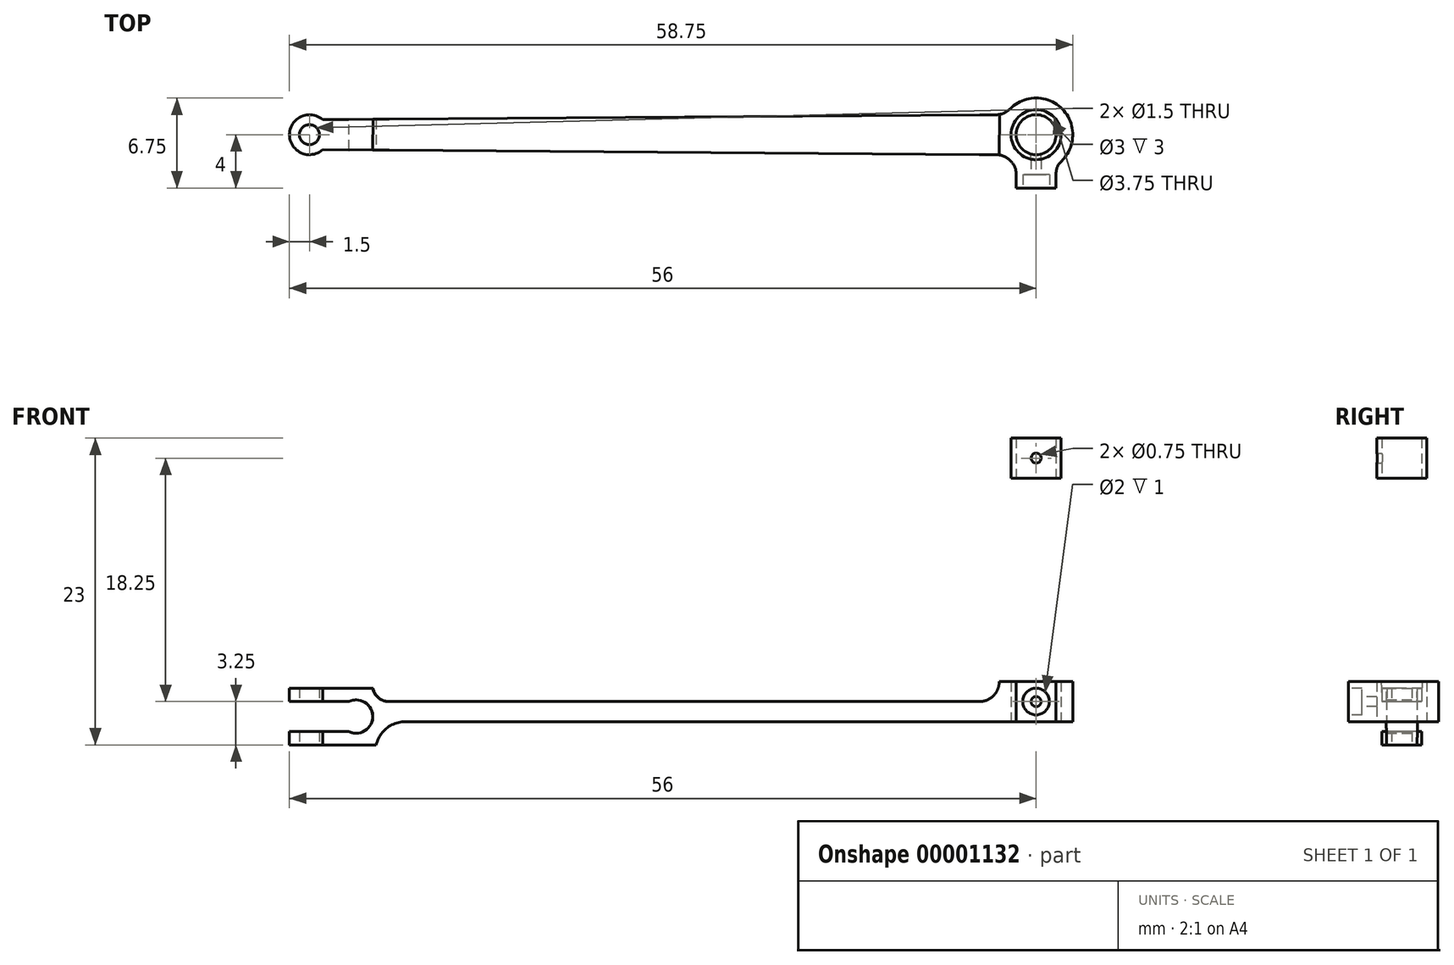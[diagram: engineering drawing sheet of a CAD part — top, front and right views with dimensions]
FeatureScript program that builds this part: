
annotation { "Feature Type Name" : "Feature", "Feature Type Description" : "" }
export const myFeature = defineFeature(function(context is Context, id is Id, definition is map)
    precondition{}
    {
        {
            var Q0;
            Q0=qCreatedBy(makeId("Top.planeOp"),FACE);
            var sketch = newSketch(context, id + "F0", { "sketchPlane" : qUnion([Q0])});
            skCircle(sketch, "E0", {"center": v(0, 0) * mm, "radius": 0.75 * mm});
            skCircle(sketch, "E1", {"center": v(54.5, 0) * mm, "radius": 1.88 * mm});
            skArc(sketch, "E2", {"start": v(1, 1.13) * mm, "mid": v(-1.5, 0) * mm, "end": v(1, -1.13) * mm});
            skArc(sketch, "E3", {"start": v(52.2, -1.5) * mm, "mid": v(52.56, -1.94) * mm, "end": v(53, -2.3) * mm});
            skLineSegment(sketch, "E4", {"start": v(1, 1.13) * mm, "end": v(52.2, 1.5) * mm});
            skLineSegment(sketch, "E5", {"start": v(1, -1.13) * mm, "end": v(52.2, -1.5) * mm});
            skLineSegment(sketch, "E6", {"start": v(53, -2.3) * mm, "end": v(53, -4) * mm});
            skLineSegment(sketch, "E7", {"start": v(53, -4) * mm, "end": v(56, -4) * mm});
            skLineSegment(sketch, "E8", {"start": v(56, -4) * mm, "end": v(56, -2.3) * mm});
            skPoint(sketch, "E9", {"position": v(54.5, -4) * mm});
            skArc(sketch, "E10.trimOffspring", {"start": v(56, -2.3) * mm, "mid": v(56.44, 1.94) * mm, "end": v(52.2, 1.5) * mm});
            skSolve(sketch);
        }
        {
            var Q0;
            Q0=makeQuery(id+"F0.imprint","IMPRINT",FACE,{"disambiguationData":[TD([[makeQuery(id+"F0.imprint","IMPRINT",EDGE,{"derivedFrom":sQuery(id+"F0.wireOp",EDGE,"E0")}),-1.0]])]});
            extrude(context, id + "F1", {"entities" : qUnion([Q0]), "depth" : 4.75 * mm});
        }
        {
            var Q0;
            Q0=makeQuery(id+"F1.opExtrude","CAP_FACE",FACE,{"disambiguationData":[OSD([sQuery(id+"F0.wireOp",EDGE,"E0"),sQuery(id+"F0.wireOp",EDGE,"E1"),sQuery(id+"F0.wireOp",EDGE,"E2"),sQuery(id+"F0.wireOp",EDGE,"E3"),sQuery(id+"F0.wireOp",EDGE,"E4"),sQuery(id+"F0.wireOp",EDGE,"E5"),sQuery(id+"F0.wireOp",EDGE,"E6"),sQuery(id+"F0.wireOp",EDGE,"E7"),sQuery(id+"F0.wireOp",EDGE,"E8"),sQuery(id+"F0.wireOp",EDGE,"E10.trimOffspring")])],"isStart":false});
            var sketch = newSketch(context, id + "F2", { "sketchPlane" : qUnion([Q0])});
            skLineSegment(sketch, "E11", {"start": v(51.74, -1.5) * mm, "end": v(51.76, 1.5) * mm});
            skLineSegment(sketch, "E12", {"start": v(4.74, -1.15) * mm, "end": v(4.76, 1.15) * mm});
            skSolve(sketch);
        }
        {
            var Q0;
            {var subQ2=sQuery(id+"F2.wireOp",EDGE,"E11");Q0=makeQuery(id+"F2.imprint","IMPRINT",FACE,{"disambiguationData":[TD([[makeQuery(id+"F2.imprint","IMPRINT",EDGE,{"derivedFrom":subQ2}),1.0]])]});}
            extrude(context, id + "F3", {"entities" : qUnion([Q0]), "operationType" : NewBodyOperationType.REMOVE, "oppositeDirection" : true, "depth" : 1.5 * mm});
        }
        {
            var Q0;
            {var subQ0=sQuery(id+"F0.wireOp",EDGE,"E0");var subQ1=sQuery(id+"F0.wireOp",EDGE,"E2");var subQ2=sQuery(id+"F0.wireOp",EDGE,"E4");var subQ3=sQuery(id+"F0.wireOp",EDGE,"E5");Q0=makeQuery(id+"F3.boolean.opBoolean","SPLIT",FACE,{"disambiguationData":[TD([makeQuery(id+"F1.opExtrude","SWEPT_FACE",FACE,{"disambiguationData":[OSD([subQ0])]})])],"derivedFrom":makeQuery(id+"F1.opExtrude","CAP_FACE",FACE,{"disambiguationData":[OSD([subQ0,sQuery(id+"F0.wireOp",EDGE,"E1"),subQ1,sQuery(id+"F0.wireOp",EDGE,"E3"),subQ2,subQ3,sQuery(id+"F0.wireOp",EDGE,"E6"),sQuery(id+"F0.wireOp",EDGE,"E7"),sQuery(id+"F0.wireOp",EDGE,"E8"),sQuery(id+"F0.wireOp",EDGE,"E10.trimOffspring")])],"isStart":false})});}
            extrude(context, id + "F4", {"entities" : qUnion([Q0]), "operationType" : NewBodyOperationType.REMOVE, "oppositeDirection" : true, "depth" : 0.5 * mm});
        }
        {
            var Q0;
            Q0=makeQuery(id+"F1.opExtrude","CAP_FACE",FACE,{"disambiguationData":[OSD([sQuery(id+"F0.wireOp",EDGE,"E0"),sQuery(id+"F0.wireOp",EDGE,"E1"),sQuery(id+"F0.wireOp",EDGE,"E2"),sQuery(id+"F0.wireOp",EDGE,"E3"),sQuery(id+"F0.wireOp",EDGE,"E4"),sQuery(id+"F0.wireOp",EDGE,"E5"),sQuery(id+"F0.wireOp",EDGE,"E6"),sQuery(id+"F0.wireOp",EDGE,"E7"),sQuery(id+"F0.wireOp",EDGE,"E8"),sQuery(id+"F0.wireOp",EDGE,"E10.trimOffspring")])],"isStart":true});
            var sketch = newSketch(context, id + "F5", { "sketchPlane" : qUnion([Q0])});
            skLineSegment(sketch, "E13", {"start": v(5, -1.15) * mm, "end": v(5, 1.15) * mm});
            skSolve(sketch);
        }
        {
            var Q0;
            {var subQ1=sQuery(id+"F5.wireOp",EDGE,"E13");Q0=makeQuery(id+"F5.imprint","IMPRINT",FACE,{"disambiguationData":[TD([[makeQuery(id+"F5.imprint","IMPRINT",EDGE,{"derivedFrom":subQ1}),-1.0]])]});}
            extrude(context, id + "F6", {"entities" : qUnion([Q0]), "operationType" : NewBodyOperationType.REMOVE, "oppositeDirection" : true, "depth" : 1.75 * mm});
        }
        {
            var Q0;
            Q0=makeQuery(id+"F3.boolean.opBoolean","COPY",EDGE,{"derivedFrom":makeQuery(id+"F3.opExtrude","CAP_EDGE",EDGE,{"disambiguationData":[OSD([sQuery(id+"F2.wireOp",EDGE,"E12")])],"isStart":false})});
            fillet(context, id + "F7", {"entities" : qUnion([Q0]), "radius" : 1.25 * mm, "tangentPropagation" : true, "allowEdgeOverflow" : false});
        }
        {
            var Q0;
            Q0=makeQuery(id+"F3.boolean.opBoolean","COPY",EDGE,{"derivedFrom":makeQuery(id+"F3.opExtrude","CAP_EDGE",EDGE,{"disambiguationData":[OSD([sQuery(id+"F2.wireOp",EDGE,"E11")])],"isStart":false})});
            fillet(context, id + "F8", {"entities" : qUnion([Q0]), "radius" : 1.5 * mm, "tangentPropagation" : true, "allowEdgeOverflow" : false});
        }
        {
            var Q0;
            Q0=makeQuery(id+"F6.boolean.opBoolean","COPY",EDGE,{"derivedFrom":makeQuery(id+"F6.opExtrude","CAP_EDGE",EDGE,{"disambiguationData":[OSD([sQuery(id+"F5.wireOp",EDGE,"E13")])],"isStart":false})});
            fillet(context, id + "F9", {"entities" : qUnion([Q0]), "radius" : 2.25 * mm, "tangentPropagation" : true, "allowEdgeOverflow" : false});
        }
        {
            var Q0;
            Q0=makeQuery(id+"F1.opExtrude","SWEPT_FACE",FACE,{"disambiguationData":[OSD([sQuery(id+"F0.wireOp",EDGE,"E4")])]});
            var sketch = newSketch(context, id + "F10", { "sketchPlane" : qUnion([Q0])});
            skLineSegment(sketch, "E14", {"start": v(-3.5, 4.25) * mm, "end": v(-3.5, 0) * mm, "construction": true});
            skPoint(sketch, "E15", {"position": v(-3.5, 2.12) * mm});
            skArc(sketch, "E16", {"start": v(-2.96, 3.25) * mm, "mid": v(-4.75, 2.12) * mm, "end": v(-2.96, 1) * mm});
            skLineSegment(sketch, "E17", {"start": v(-2.96, 3.25) * mm, "end": v(1.72, 3.25) * mm});
            skLineSegment(sketch, "E18", {"start": v(1.72, 3.25) * mm, "end": v(1.72, 1) * mm});
            skLineSegment(sketch, "E19", {"start": v(1.72, 1) * mm, "end": v(-2.96, 1) * mm});
            skPoint(sketch, "E20", {"position": v(1.72, 2.13) * mm});
            skSolve(sketch);
        }
        {
            var Q0;
            {var subQ5=sQuery(id+"F10.wireOp",EDGE,"E18");Q0=makeQuery(id+"F10.imprint","IMPRINT",FACE,{"disambiguationData":[TD([[makeQuery(id+"F10.imprint","IMPRINT",EDGE,{"derivedFrom":subQ5}),-1.0]])]});}
            var Q1;
            {var subQ5=sQuery(id+"F10.wireOp",EDGE,"E16");Q1=makeQuery(id+"F10.imprint","IMPRINT",FACE,{"disambiguationData":[TD([[makeQuery(id+"F10.imprint","IMPRINT",EDGE,{"derivedFrom":subQ5}),1.0]])]});}
            extrude(context, id + "F11", {"entities" : qUnion([Q0, Q1]), "operationType" : NewBodyOperationType.REMOVE, "endBound" : BoundingType.SYMMETRIC, "oppositeDirection" : true, "depth" : 25 * mm});
        }
        {
            var Q0;
            Q0=makeQuery(id+"F1.opExtrude","SWEPT_FACE",FACE,{"disambiguationData":[OSD([sQuery(id+"F0.wireOp",EDGE,"E7")])]});
            var sketch = newSketch(context, id + "F12", { "sketchPlane" : qUnion([Q0])});
            skPoint(sketch, "E21", {"position": v(53, 3.25) * mm});
            skPoint(sketch, "E22", {"position": v(54.5, 4.75) * mm});
            skCircle(sketch, "E23", {"center": v(54.5, 3.25) * mm, "radius": 1 * mm});
            skCircle(sketch, "E24", {"center": v(54.5, 3.25) * mm, "radius": 0.38 * mm});
            skSolve(sketch);
        }
        {
            var Q0;
            Q0=makeQuery(id+"F12.imprint","IMPRINT",FACE,{"disambiguationData":[TD([[makeQuery(id+"F12.imprint","IMPRINT",EDGE,{"derivedFrom":sQuery(id+"F12.wireOp",EDGE,"E23")}),1.0]])]});
            extrude(context, id + "F13", {"entities" : qUnion([Q0]), "operationType" : NewBodyOperationType.REMOVE, "oppositeDirection" : true, "depth" : 1 * mm});
        }
        {
            var Q0;
            Q0=makeQuery(id+"F13.boolean.opBoolean","SPLIT",FACE,{"disambiguationData":[TD([makeQuery(id+"F13.opExtrude","SWEPT_FACE",FACE,{"disambiguationData":[OSD([sQuery(id+"F12.wireOp",EDGE,"E24")])]})])],"derivedFrom":makeQuery(id+"F1.opExtrude","SWEPT_FACE",FACE,{"disambiguationData":[OSD([sQuery(id+"F0.wireOp",EDGE,"E7")])]})});
            var Q1;
            Q1=makeQuery(id+"F1.opExtrude","SWEPT_BODY",BODY,{"disambiguationData":[OSD([sQuery(id+"F0.wireOp",EDGE,"E0"),sQuery(id+"F0.wireOp",EDGE,"E1"),sQuery(id+"F0.wireOp",EDGE,"E2"),sQuery(id+"F0.wireOp",EDGE,"E3"),sQuery(id+"F0.wireOp",EDGE,"E4"),sQuery(id+"F0.wireOp",EDGE,"E5"),sQuery(id+"F0.wireOp",EDGE,"E6"),sQuery(id+"F0.wireOp",EDGE,"E7"),sQuery(id+"F0.wireOp",EDGE,"E8"),sQuery(id+"F0.wireOp",EDGE,"E10.trimOffspring")])]});
            extrude(context, id + "F14", {"entities" : qUnion([Q0]), "operationType" : NewBodyOperationType.REMOVE, "endBound" : BoundingType.UP_TO_BODY, "oppositeDirection" : true, "endBoundEntityBody" : qUnion([Q1]), "depth" : 25 * mm});
        }
        {
            var Q0;
            Q0=makeQuery(id+"F1.opExtrude","SWEPT_EDGE",EDGE,{"disambiguationData":[OSD([sQuery(id+"F0.wireOp",EDGE,"E3"),sQuery(id+"F0.wireOp",EDGE,"E6")])]});
            var Q1;
            Q1=makeQuery(id+"F1.opExtrude","SWEPT_EDGE",EDGE,{"disambiguationData":[OSD([sQuery(id+"F0.wireOp",EDGE,"E8"),sQuery(id+"F0.wireOp",EDGE,"E10.trimOffspring")])]});
            fillet(context, id + "F15", {"entities" : qUnion([Q0, Q1]), "radius" : 1.25 * mm, "tangentPropagation" : true, "allowEdgeOverflow" : false});
        }
        {
            var Q0;
            Q0=makeQuery(id+"F1.opExtrude","SWEPT_EDGE",EDGE,{"disambiguationData":[OSD([sQuery(id+"F0.wireOp",EDGE,"E4"),sQuery(id+"F0.wireOp",EDGE,"E10.trimOffspring")])]});
            var Q1;
            Q1=makeQuery(id+"F1.opExtrude","SWEPT_EDGE",EDGE,{"disambiguationData":[OSD([sQuery(id+"F0.wireOp",EDGE,"E3"),sQuery(id+"F0.wireOp",EDGE,"E5")])]});
            fillet(context, id + "F16", {"entities" : qUnion([Q0, Q1]), "radius" : 1.5 * mm, "tangentPropagation" : true, "allowEdgeOverflow" : false});
        }
        {
            var Q0;
            Q0=qCreatedBy(makeId("Top.planeOp"),FACE);
            cPlane(context, id + "F17", {"entities" : qUnion([Q0]), "cplaneType" : CPlaneType.OFFSET, "offset" : 20 * mm, "width" : 150 * mm, "height" : 150 * mm});
        }
        {
            var Q0;
            Q0=qCreatedBy(id+"F17.planeOp",FACE);
            var sketch = newSketch(context, id + "F18", { "sketchPlane" : qUnion([Q0])});
            skLineSegment(sketch, "E25", {"start": v(0, 0) * mm, "end": v(54.5, 0) * mm, "construction": true});
            skCircle(sketch, "E26", {"center": v(54.5, 0) * mm, "radius": 1.88 * mm});
            skCircle(sketch, "E27", {"center": v(54.5, 0) * mm, "radius": 1.5 * mm});
            skSolve(sketch);
        }
        {
            var Q0;
            Q0=makeQuery(id+"F18.imprint","IMPRINT",FACE,{"disambiguationData":[TD([[makeQuery(id+"F18.imprint","IMPRINT",EDGE,{"derivedFrom":sQuery(id+"F18.wireOp",EDGE,"E26")}),1.0]])]});
            extrude(context, id + "F19", {"entities" : qUnion([Q0]), "depth" : 3 * mm});
        }
        {
            var Q0;
            Q0=qCreatedBy(makeId("Front.planeOp"),FACE);
            var sketch = newSketch(context, id + "F20", { "sketchPlane" : qUnion([Q0])});
            skLineSegment(sketch, "E28", {"start": v(0, 0) * mm, "end": v(0, 21.5) * mm, "construction": true});
            skLineSegment(sketch, "E29", {"start": v(0, 21.5) * mm, "end": v(54.5, 21.5) * mm, "construction": true});
            skCircle(sketch, "E30", {"center": v(54.5, 21.5) * mm, "radius": 0.38 * mm});
            skSolve(sketch);
        }
        {
            var Q0;
            Q0=makeQuery(id+"F20.imprint","IMPRINT",FACE,{"disambiguationData":[TD([[makeQuery(id+"F20.imprint","IMPRINT",EDGE,{"derivedFrom":sQuery(id+"F20.wireOp",EDGE,"E30")}),1.0]])]});
            extrude(context, id + "F21", {"entities" : qUnion([Q0]), "operationType" : NewBodyOperationType.REMOVE, "depth" : 25 * mm});
        }
    });
